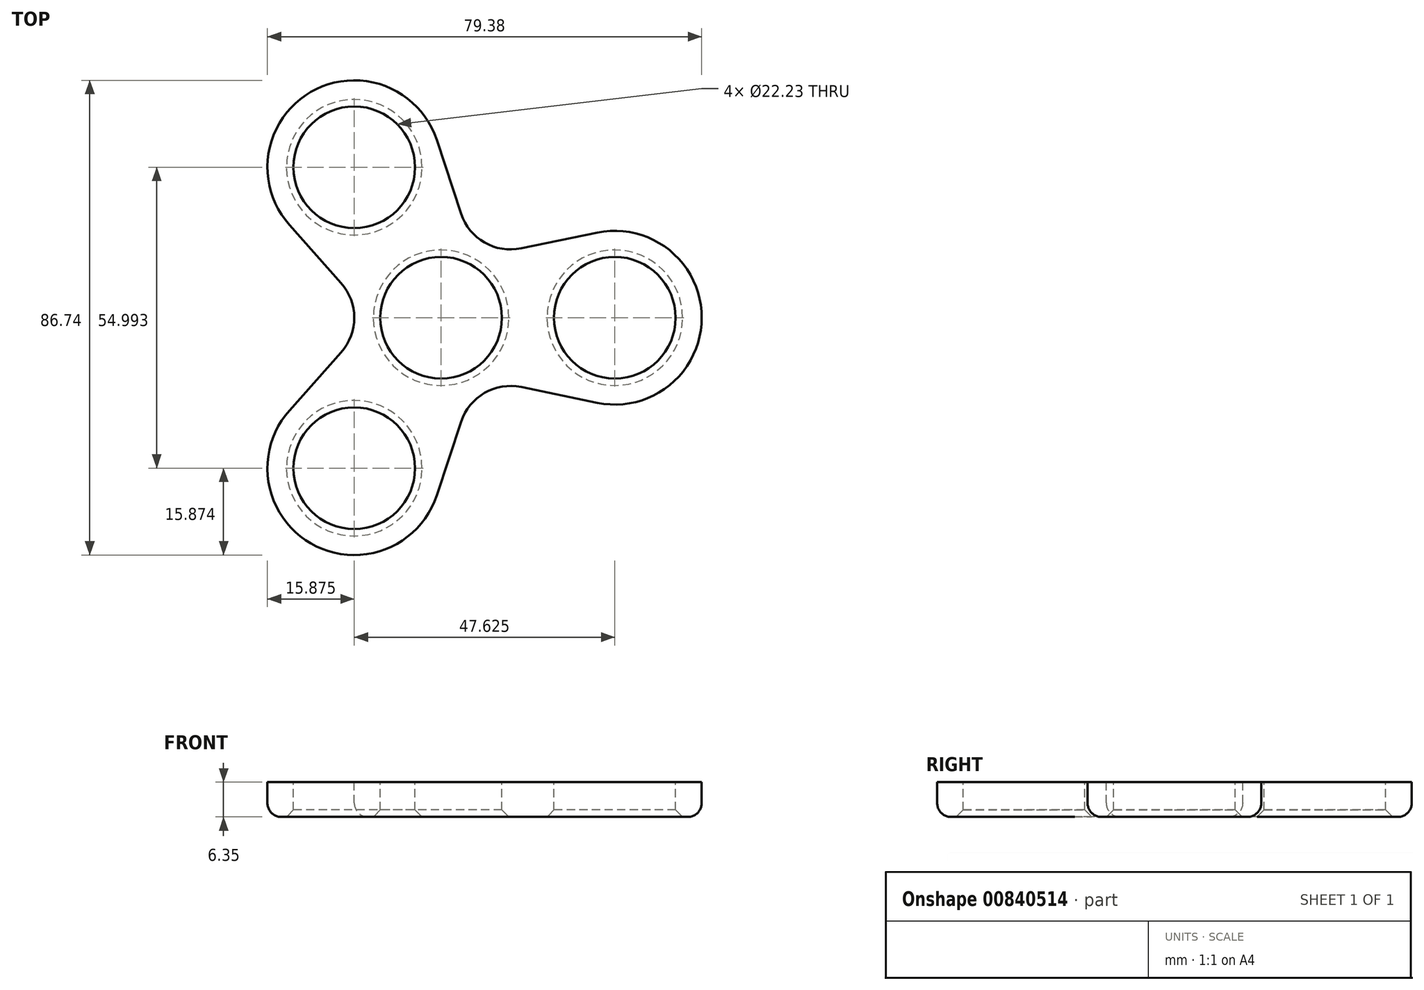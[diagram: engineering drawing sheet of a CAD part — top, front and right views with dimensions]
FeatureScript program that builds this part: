
annotation { "Feature Type Name" : "Feature", "Feature Type Description" : "" }
export const myFeature = defineFeature(function(context is Context, id is Id, definition is map)
    precondition{}
    {
        {
            var Q0;
            Q0=qCreatedBy(makeId("Top.planeOp"),FACE);
            var sketch = newSketch(context, id + "F0", { "sketchPlane" : qUnion([Q0])});
            skCircle(sketch, "E0", {"center": v(0, 0) * mm, "radius": 47.63 * mm});
            skSolve(sketch);
        }
        {
            var Q0;
            Q0=makeQuery(id+"F0.imprint","IMPRINT",FACE,{"disambiguationData":[TD([[makeQuery(id+"F0.imprint","IMPRINT",EDGE,{"derivedFrom":sQuery(id+"F0.wireOp",EDGE,"E0")}),1.0]])]});
            extrude(context, id + "F1", {"entities" : qUnion([Q0]), "depth" : 6.35 * mm, "offsetDistance" : 25.4 * mm});
        }
        {
            var Q0;
            Q0=makeQuery(id+"F1.opExtrude","CAP_FACE",FACE,{"disambiguationData":[OSD([sQuery(id+"F0.wireOp",EDGE,"E0")])],"isStart":false});
            var sketch = newSketch(context, id + "F2", { "sketchPlane" : qUnion([Q0])});
            skCircle(sketch, "E1", {"center": v(0, 0) * mm, "radius": 11.11 * mm});
            skCircle(sketch, "E2", {"center": v(0, 0) * mm, "radius": 42.86 * mm, "construction": true});
            skCircle(sketch, "E3", {"center": v(31.75, 0) * mm, "radius": 11.11 * mm});
            skLineSegment(sketch, "E4", {"start": v(0, 0) * mm, "end": v(-21.43, -37.12) * mm, "construction": true});
            skCircle(sketch, "E5", {"center": v(-15.87, -27.5) * mm, "radius": 11.11 * mm});
            skLineSegment(sketch, "E6", {"start": v(0, 0) * mm, "end": v(-21.43, 37.12) * mm, "construction": true});
            skCircle(sketch, "E7", {"center": v(-15.88, 27.5) * mm, "radius": 11.11 * mm});
            skSolve(sketch);
        }
        {
            var Q0;
            Q0=makeQuery(id+"F2.imprint","IMPRINT",FACE,{"disambiguationData":[TD([[makeQuery(id+"F2.imprint","IMPRINT",EDGE,{"derivedFrom":sQuery(id+"F2.wireOp",EDGE,"E5")}),1.0]])]});
            var Q1;
            Q1=makeQuery(id+"F2.imprint","IMPRINT",FACE,{"disambiguationData":[TD([[makeQuery(id+"F2.imprint","IMPRINT",EDGE,{"derivedFrom":sQuery(id+"F2.wireOp",EDGE,"E1")}),1.0]])]});
            var Q2;
            Q2=makeQuery(id+"F2.imprint","IMPRINT",FACE,{"disambiguationData":[TD([[makeQuery(id+"F2.imprint","IMPRINT",EDGE,{"derivedFrom":sQuery(id+"F2.wireOp",EDGE,"E3")}),1.0]])]});
            var Q3;
            Q3=makeQuery(id+"F2.imprint","IMPRINT",FACE,{"disambiguationData":[TD([[makeQuery(id+"F2.imprint","IMPRINT",EDGE,{"derivedFrom":sQuery(id+"F2.wireOp",EDGE,"E7")}),1.0]])]});
            extrude(context, id + "F3", {"entities" : qUnion([Q0, Q1, Q2, Q3]), "operationType" : NewBodyOperationType.REMOVE, "endBound" : BoundingType.THROUGH_ALL, "oppositeDirection" : true, "depth" : 25.4 * mm, "offsetDistance" : 25.4 * mm});
        }
        {
            var Q0;
            Q0=makeQuery(id+"F1.opExtrude","CAP_FACE",FACE,{"disambiguationData":[OSD([sQuery(id+"F0.wireOp",EDGE,"E0")])],"isStart":false});
            var sketch = newSketch(context, id + "F4", { "sketchPlane" : qUnion([Q0])});
            skLineSegment(sketch, "E8", {"start": v(0, 0) * mm, "end": v(18.26, -31.62) * mm, "construction": true});
            skCircle(sketch, "E9", {"center": v(0, 0) * mm, "radius": 15.88 * mm, "construction": true});
            skCircle(sketch, "E10", {"center": v(0, 0) * mm, "radius": 36.51 * mm, "construction": true});
            skCircle(sketch, "E11", {"center": v(12.7, -22) * mm, "radius": 9.53 * mm});
            skCircle(sketch, "E12", {"center": v(-25.4, 0) * mm, "radius": 9.53 * mm});
            skLineSegment(sketch, "E13", {"start": v(0, 0) * mm, "end": v(18.26, 31.62) * mm, "construction": true});
            skCircle(sketch, "E14", {"center": v(12.7, 22) * mm, "radius": 9.53 * mm});
            skSolve(sketch);
        }
        {
            var Q0;
            Q0=makeQuery(id+"F4.imprint","IMPRINT",FACE,{"disambiguationData":[TD([[makeQuery(id+"F4.imprint","IMPRINT",EDGE,{"derivedFrom":sQuery(id+"F4.wireOp",EDGE,"E14")}),1.0]])]});
            var Q1;
            Q1=makeQuery(id+"F4.imprint","IMPRINT",FACE,{"disambiguationData":[TD([[makeQuery(id+"F4.imprint","IMPRINT",EDGE,{"derivedFrom":sQuery(id+"F4.wireOp",EDGE,"E12")}),1.0]])]});
            var Q2;
            Q2=makeQuery(id+"F4.imprint","IMPRINT",FACE,{"disambiguationData":[TD([[makeQuery(id+"F4.imprint","IMPRINT",EDGE,{"derivedFrom":sQuery(id+"F4.wireOp",EDGE,"E11")}),1.0]])]});
            extrude(context, id + "F5", {"entities" : qUnion([Q0, Q1, Q2]), "operationType" : NewBodyOperationType.REMOVE, "endBound" : BoundingType.THROUGH_ALL, "oppositeDirection" : true, "depth" : 25.4 * mm, "offsetDistance" : 25.4 * mm});
        }
        {
            var Q0;
            Q0=makeQuery(id+"F1.opExtrude","CAP_FACE",FACE,{"disambiguationData":[OSD([sQuery(id+"F0.wireOp",EDGE,"E0")])],"isStart":false});
            var sketch = newSketch(context, id + "F6", { "sketchPlane" : qUnion([Q0])});
            skArc(sketch, "E15", {"start": v(28.53, -15.55) * mm, "mid": v(47.63, 0) * mm, "end": v(28.53, 15.55) * mm});
            skArc(sketch, "E16", {"start": v(-27.73, -16.94) * mm, "mid": v(-23.81, -41.24) * mm, "end": v(-0.8, -32.48) * mm});
            skArc(sketch, "E17", {"start": v(-0.8, 32.48) * mm, "mid": v(-23.81, 41.24) * mm, "end": v(-27.73, 16.94) * mm});
            skLineSegment(sketch, "E18", {"start": v(3.66, 19) * mm, "end": v(-0.8, 32.48) * mm});
            skLineSegment(sketch, "E19", {"start": v(-27.73, 16.94) * mm, "end": v(-18.29, 6.33) * mm});
            skLineSegment(sketch, "E20", {"start": v(-27.73, -16.94) * mm, "end": v(-18.29, -6.33) * mm});
            skLineSegment(sketch, "E21", {"start": v(-0.8, -32.48) * mm, "end": v(3.66, -19) * mm});
            skLineSegment(sketch, "E22", {"start": v(14.63, -12.67) * mm, "end": v(31.59, -16.18) * mm});
            skLineSegment(sketch, "E23", {"start": v(14.63, 12.67) * mm, "end": v(28.53, 15.55) * mm});
            skCircle(sketch, "E24", {"center": v(0, 0) * mm, "radius": 56.66 * mm});
            skSolve(sketch);
        }
        {
            var Q0;
            {var subQ6=sQuery(id+"F6.wireOp",EDGE,"E19");Q0=makeQuery(id+"F6.imprint","IMPRINT",FACE,{"disambiguationData":[TD([[makeQuery(id+"F6.imprint","IMPRINT",EDGE,{"derivedFrom":subQ6}),-1.0]])]});}
            var Q1;
            {var subQ0=sQuery(id+"F6.wireOp",EDGE,"E21");Q1=makeQuery(id+"F6.imprint","IMPRINT",FACE,{"disambiguationData":[TD([[makeQuery(id+"F6.imprint","IMPRINT",EDGE,{"derivedFrom":subQ0}),-1.0]])]});}
            var Q2;
            {var subQ0=sQuery(id+"F6.wireOp",EDGE,"E18");Q2=makeQuery(id+"F6.imprint","IMPRINT",FACE,{"disambiguationData":[TD([[makeQuery(id+"F6.imprint","IMPRINT",EDGE,{"derivedFrom":subQ0}),-1.0]])]});}
            var Q3;
            Q3=makeQuery(id+"F6.imprint","IMPRINT",FACE,{"disambiguationData":[TD([[makeQuery(id+"F6.imprint","IMPRINT",EDGE,{"derivedFrom":sQuery(id+"F6.wireOp",EDGE,"E24")}),1.0]])]});
            extrude(context, id + "F7", {"entities" : qUnion([Q0, Q1, Q2, Q3]), "operationType" : NewBodyOperationType.REMOVE, "endBound" : BoundingType.THROUGH_ALL, "oppositeDirection" : true, "depth" : 25.4 * mm, "offsetDistance" : 25.4 * mm});
        }
        {
            var Q0;
            Q0=makeQuery(id+"F7.boolean.opBoolean","COPY",EDGE,{"derivedFrom":makeQuery(id+"F7.opExtrude","CAP_EDGE",EDGE,{"disambiguationData":[OSD([sQuery(id+"F6.wireOp",EDGE,"E16")])],"isStart":true})});
            var Q1;
            Q1=makeQuery(id+"F7.boolean.opBoolean","COPY",EDGE,{"derivedFrom":makeQuery(id+"F7.opExtrude","CAP_EDGE",EDGE,{"disambiguationData":[OSD([sQuery(id+"F6.wireOp",EDGE,"E21")])],"isStart":true})});
            var Q2;
            Q2=makeQuery(id+"F5.boolean.opBoolean","INTERSECT",EDGE,{"derivedFrom":[makeQuery(id+"F1.opExtrude","CAP_FACE",FACE,{"disambiguationData":[OSD([sQuery(id+"F0.wireOp",EDGE,"E0")])],"isStart":true}),makeQuery(id+"F5.opExtrude","SWEPT_FACE",FACE,{"disambiguationData":[OSD([sQuery(id+"F4.wireOp",EDGE,"E11")])]})]});
            fillet(context, id + "F8", {"entities" : qUnion([Q0, Q1, Q2]), "radius" : 2.54 * mm, "tangentPropagation" : true, "allowEdgeOverflow" : false});
        }
        {
            var Q0;
            Q0=makeQuery(id+"F3.boolean.opBoolean","COPY",EDGE,{"derivedFrom":makeQuery(id+"F3.opExtrude","CAP_EDGE",EDGE,{"disambiguationData":[OSD([sQuery(id+"F2.wireOp",EDGE,"E5")])],"isStart":true})});
            var Q1;
            Q1=makeQuery(id+"F3.boolean.opBoolean","INTERSECT",EDGE,{"derivedFrom":[makeQuery(id+"F1.opExtrude","CAP_FACE",FACE,{"disambiguationData":[OSD([sQuery(id+"F0.wireOp",EDGE,"E0")])],"isStart":true}),makeQuery(id+"F3.opExtrude","SWEPT_FACE",FACE,{"disambiguationData":[OSD([sQuery(id+"F2.wireOp",EDGE,"E5")])]})]});
            var Q2;
            Q2=makeQuery(id+"F3.boolean.opBoolean","INTERSECT",EDGE,{"derivedFrom":[makeQuery(id+"F1.opExtrude","CAP_FACE",FACE,{"disambiguationData":[OSD([sQuery(id+"F0.wireOp",EDGE,"E0")])],"isStart":true}),makeQuery(id+"F3.opExtrude","SWEPT_FACE",FACE,{"disambiguationData":[OSD([sQuery(id+"F2.wireOp",EDGE,"E1")])]})]});
            var Q3;
            Q3=makeQuery(id+"F3.boolean.opBoolean","COPY",EDGE,{"derivedFrom":makeQuery(id+"F3.opExtrude","CAP_EDGE",EDGE,{"disambiguationData":[OSD([sQuery(id+"F2.wireOp",EDGE,"E1")])],"isStart":true})});
            var Q4;
            Q4=makeQuery(id+"F3.boolean.opBoolean","INTERSECT",EDGE,{"derivedFrom":[makeQuery(id+"F1.opExtrude","CAP_FACE",FACE,{"disambiguationData":[OSD([sQuery(id+"F0.wireOp",EDGE,"E0")])],"isStart":true}),makeQuery(id+"F3.opExtrude","SWEPT_FACE",FACE,{"disambiguationData":[OSD([sQuery(id+"F2.wireOp",EDGE,"E7")])]})]});
            var Q5;
            Q5=makeQuery(id+"F3.boolean.opBoolean","COPY",EDGE,{"derivedFrom":makeQuery(id+"F3.opExtrude","CAP_EDGE",EDGE,{"disambiguationData":[OSD([sQuery(id+"F2.wireOp",EDGE,"E7")])],"isStart":true})});
            var Q6;
            Q6=makeQuery(id+"F3.boolean.opBoolean","INTERSECT",EDGE,{"derivedFrom":[makeQuery(id+"F1.opExtrude","CAP_FACE",FACE,{"disambiguationData":[OSD([sQuery(id+"F0.wireOp",EDGE,"E0")])],"isStart":true}),makeQuery(id+"F3.opExtrude","SWEPT_FACE",FACE,{"disambiguationData":[OSD([sQuery(id+"F2.wireOp",EDGE,"E3")])]})]});
            var Q7;
            Q7=makeQuery(id+"F3.boolean.opBoolean","COPY",EDGE,{"derivedFrom":makeQuery(id+"F3.opExtrude","CAP_EDGE",EDGE,{"disambiguationData":[OSD([sQuery(id+"F2.wireOp",EDGE,"E3")])],"isStart":true})});
            chamfer(context, id + "F9", {"entities" : qUnion([Q0, Q1, Q2, Q3, Q4, Q5, Q6, Q7]), "width" : 1.27 * mm, "tangentPropagation" : true});
        }
        {
            var Q0;
            Q0=makeQuery(id+"F1.opExtrude","SWEPT_BODY",BODY,{"disambiguationData":[OSD([sQuery(id+"F0.wireOp",EDGE,"E0")])]});
            transform(context, id + "F10", {"entities" : qUnion([Q0]), "transformType" : TransformType.TRANSLATION_3D, "dx" : 76.2 * mm, "dy" : 0 * mm, "dz" : 0 * mm, "makeCopy" : true});
        }
        {
            var Q0;
            Q0=makeQuery(id+"F10.opPattern","COPY",BODY,{"derivedFrom":makeQuery(id+"F1.opExtrude","SWEPT_BODY",BODY,{"disambiguationData":[OSD([sQuery(id+"F0.wireOp",EDGE,"E0")])]}),"instanceName":"1"});
            deleteBodies(context, id + "F11", {"entities" : qUnion([Q0])});
        }
    });
